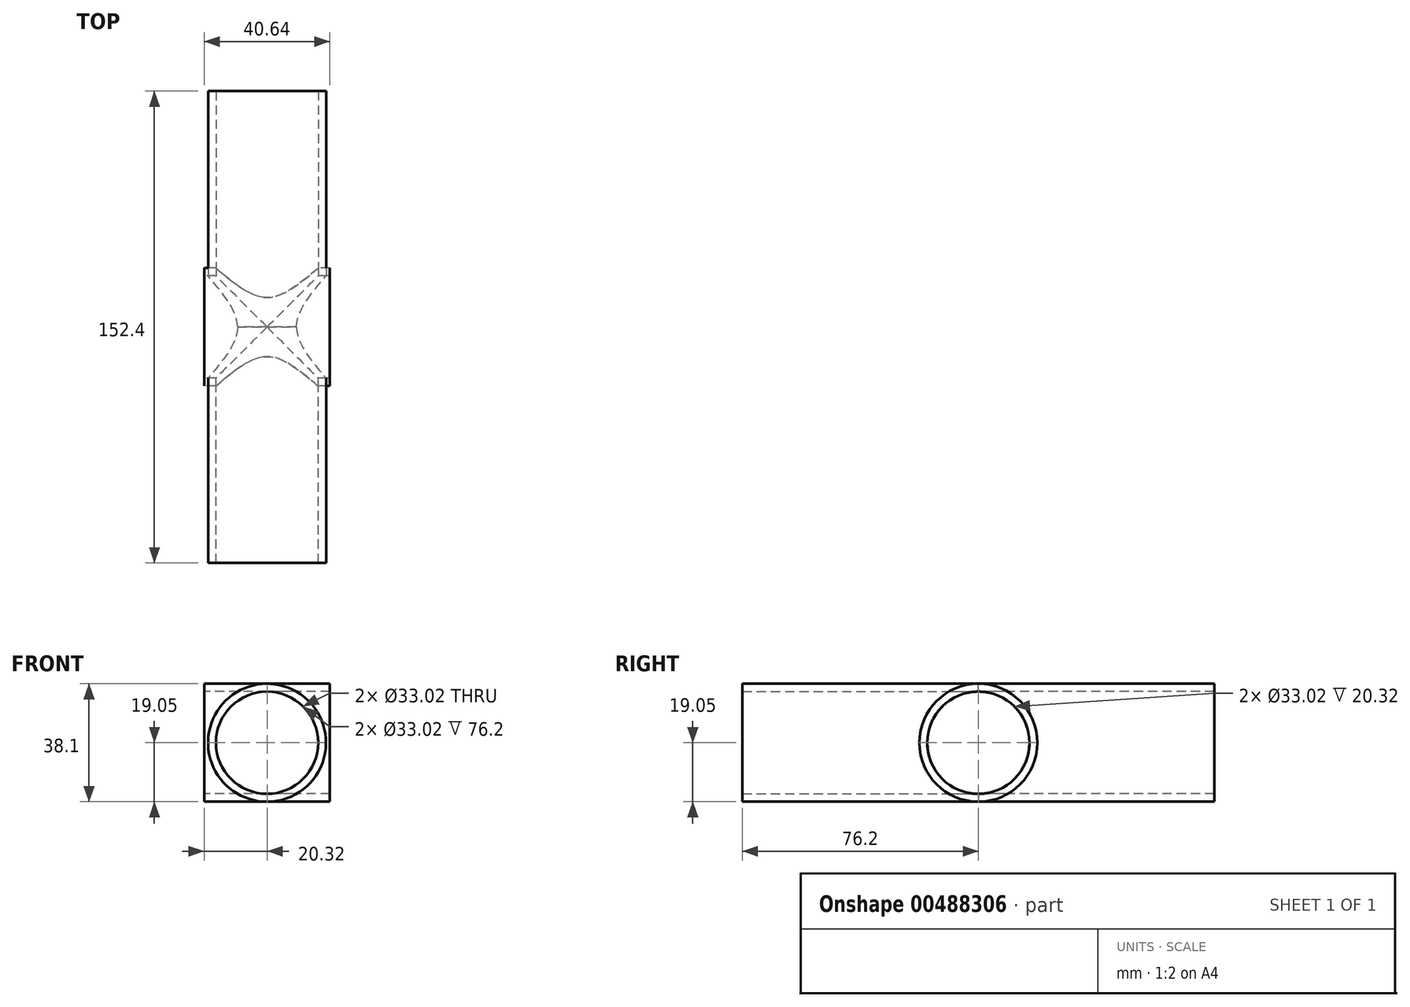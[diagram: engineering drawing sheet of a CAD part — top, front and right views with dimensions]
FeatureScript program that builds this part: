
annotation { "Feature Type Name" : "Feature", "Feature Type Description" : "" }
export const myFeature = defineFeature(function(context is Context, id is Id, definition is map)
    precondition{}
    {
        {
            var Q0;
            Q0=qCreatedBy(makeId("Front.planeOp"),FACE);
            var sketch = newSketch(context, id + "F0", { "sketchPlane" : qUnion([Q0])});
            skCircle(sketch, "E0", {"center": v(0, 0) * mm, "radius": 19.05 * mm});
            skSolve(sketch);
        }
        {
            var Q0;
            Q0=makeQuery(id+"F0.imprint","IMPRINT",FACE,{"disambiguationData":[TD([[makeQuery(id+"F0.imprint","IMPRINT",EDGE,{"derivedFrom":sQuery(id+"F0.wireOp",EDGE,"E0")}),1.0]])]});
            extrude(context, id + "F1", {"entities" : qUnion([Q0]), "depth" : 76.2 * mm});
        }
        {
            var Q0;
            Q0=qCreatedBy(makeId("Right.planeOp"),FACE);
            var sketch = newSketch(context, id + "F2", { "sketchPlane" : qUnion([Q0])});
            skCircle(sketch, "E1", {"center": v(0, 0) * mm, "radius": 19.05 * mm});
            skSolve(sketch);
        }
        {
            var Q0;
            Q0=makeQuery(id+"F2.imprint","IMPRINT",FACE,{"disambiguationData":[TD([[makeQuery(id+"F2.imprint","IMPRINT",EDGE,{"derivedFrom":sQuery(id+"F2.wireOp",EDGE,"E1")}),1.0]])]});
            extrude(context, id + "F3", {"entities" : qUnion([Q0]), "endBound" : BoundingType.SYMMETRIC, "depth" : 40.64 * mm});
        }
        {
            var Q0;
            Q0=qSketchRegion(id+"F0",true);
            var Q1;
            Q1=sQuery(id+"F0.wireOp",EDGE,"E0");
            extrude(context, id + "F4", {"entities" : qUnion([Q0]), "surfaceEntities" : qUnion([Q1]), "oppositeDirection" : true, "depth" : 76.2 * mm});
        }
        {
            var Q0;
            Q0=sQuery(id+"F2.wireOp",VERTEX,"E1.center");
            var Q1;
            Q1=makeQuery(id+"F1.opExtrude","SWEPT_BODY",BODY,{"disambiguationData":[OSD([sQuery(id+"F0.wireOp",EDGE,"E0")])]});
            var Q2;
            Q2=makeQuery(id+"F3.opExtrude","SWEPT_BODY",BODY,{"disambiguationData":[OSD([sQuery(id+"F2.wireOp",EDGE,"E1")])]});
            var Q3;
            Q3=makeQuery(id+"F4.opExtrude","SWEPT_BODY",BODY,{"disambiguationData":[OSD([sQuery(id+"F0.wireOp",EDGE,"E0")])]});
            hole(context, id + "F5", {"style" : HoleStyle.SIMPLE, "endStyle" : HoleEndStyle.THROUGH, "oppositeDirection" : true, "holeDiameter" : 33.02 * mm, "isTappedThrough" : true, "tappedDepth" : 12.7 * mm, "tapClearance" : 3, "startFromSketch" : true, "locations" : qUnion([Q0]), "scope" : qUnion([Q1, Q2, Q3])});
        }
        {
            var Q0;
            Q0=sQuery(id+"F2.wireOp",VERTEX,"E1.center");
            var Q1;
            Q1=makeQuery(id+"F1.opExtrude","SWEPT_BODY",BODY,{"disambiguationData":[OSD([sQuery(id+"F0.wireOp",EDGE,"E0")])]});
            var Q2;
            Q2=makeQuery(id+"F3.opExtrude","SWEPT_BODY",BODY,{"disambiguationData":[OSD([sQuery(id+"F2.wireOp",EDGE,"E1")])]});
            var Q3;
            Q3=makeQuery(id+"F4.opExtrude","SWEPT_BODY",BODY,{"disambiguationData":[OSD([sQuery(id+"F0.wireOp",EDGE,"E0")])]});
            hole(context, id + "F6", {"style" : HoleStyle.SIMPLE, "endStyle" : HoleEndStyle.THROUGH, "holeDiameter" : 33.02 * mm, "isTappedThrough" : true, "tappedDepth" : 12.7 * mm, "tapClearance" : 3, "startFromSketch" : true, "locations" : qUnion([Q0]), "scope" : qUnion([Q1, Q2, Q3])});
        }
        {
            var Q0;
            Q0=sQuery(id+"F0.wireOp",VERTEX,"E0.center");
            var Q1;
            Q1=makeQuery(id+"F3.opExtrude","SWEPT_BODY",BODY,{"disambiguationData":[OSD([sQuery(id+"F2.wireOp",EDGE,"E1")])]});
            var Q2;
            Q2=makeQuery(id+"F1.opExtrude","SWEPT_BODY",BODY,{"disambiguationData":[OSD([sQuery(id+"F0.wireOp",EDGE,"E0")])]});
            hole(context, id + "F7", {"style" : HoleStyle.SIMPLE, "endStyle" : HoleEndStyle.THROUGH, "oppositeDirection" : true, "holeDiameter" : 33.02 * mm, "isTappedThrough" : true, "tappedDepth" : 12.7 * mm, "tapClearance" : 3, "locations" : qUnion([Q0]), "scope" : qUnion([Q1, Q2])});
        }
        {
            var Q0;
            Q0=sQuery(id+"F0.wireOp",VERTEX,"E0.center");
            var Q1;
            Q1=makeQuery(id+"F4.opExtrude","SWEPT_BODY",BODY,{"disambiguationData":[OSD([sQuery(id+"F0.wireOp",EDGE,"E0")])]});
            var Q2;
            Q2=makeQuery(id+"F3.opExtrude","SWEPT_BODY",BODY,{"disambiguationData":[OSD([sQuery(id+"F2.wireOp",EDGE,"E1")])]});
            hole(context, id + "F8", {"style" : HoleStyle.SIMPLE, "endStyle" : HoleEndStyle.THROUGH, "holeDiameter" : 33.02 * mm, "isTappedThrough" : true, "tappedDepth" : 12.7 * mm, "tapClearance" : 3, "locations" : qUnion([Q0]), "scope" : qUnion([Q1, Q2])});
        }
    });
